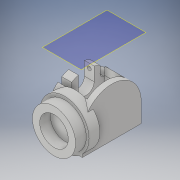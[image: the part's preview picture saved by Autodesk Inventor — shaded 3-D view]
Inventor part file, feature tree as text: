
AUTODESK INVENTOR PART (.ipt)
format: ipt  version: 2018 (Build 220112000, 112)  size: 247,296 bytes
history: native  units: in
note: dims shown in document units (in); Inventor stores cm internally (conversion verified against a paired STEP export)
features: sketch x11, extrude x10, plane x1
ambient origin geometry x8: Origin, YZ Plane, XZ Plane, XY Plane, X Axis, Y Axis, Z Axis, Center Point
bodies: Solid1 (feature_tree)
feature tree (22):
  sketch  "Sketch1"  dims[d2=0.5906in d3=1.1811in]
  extrude  "Extrusion1"  Depth=0.5906in
  extrude  "Extrusion3"  Depth=0.1969in
  extrude  "Extrusion4"  Depth=0.5906in
  extrude  "Extrusion5"  Depth=0.748in
  extrude  "Extrusion6"  Depth=0.3937in
  extrude  "Extrusion7"  Depth=0.1181in
  extrude  "Extrusion8"  Depth=0.0394in
  plane  "Work Plane1"
  extrude  "Extrusion13"  Depth=0.1181in TaperAngle=0.0deg
  sketch  "Sketch13"  dims[d34=0.1969in d35=0.0in d36=-1.5748in]
  extrude  "Extrusion16"  Depth=0.5906in
  extrude  "Extrusion17"  [1 undecoded]
  sketch  "Sketch2"  dims[d4=0.1969in d5=0.0in d12=0.1969in]
  sketch  "Sketch5"  dims[d13=0.5906in d14=0.0in d15=0.2953in]
  sketch  "Sketch6"  dims[d16=0.374in d17=0.748in]
  sketch  "Sketch7"  dims[d18=0.3937in d19=0.0in d20=0.315in]
  sketch  "Sketch8"  dims[d21=0.1181in d22=0.0787in]
  sketch  "Sketch9"  dims[d23=0.1969in d24=0.0in d27=0.0394in]
  sketch  "Sketch10"  dims[d28=0.1181in d29=0.0in d30=0.1181in d31=0.0in]
  sketch  "Sketch11"  dims[d32=0.5906in d33=0.5906in]
  sketch  "Sketch16"  dims[d40=0.0787in d52=0.2362in d53=0.0in d54=0.0in d63=0.8661in d64=0.5748in d73=0.2165in d74=0.0in d75=0.2165in d76=0.0in d77=0.9843in]
note: 1 required parameter value undecoded (feature->parameter linkage not recoverable at this tier; creation-order binding heuristic only, values carry confidence <= 0.55)
